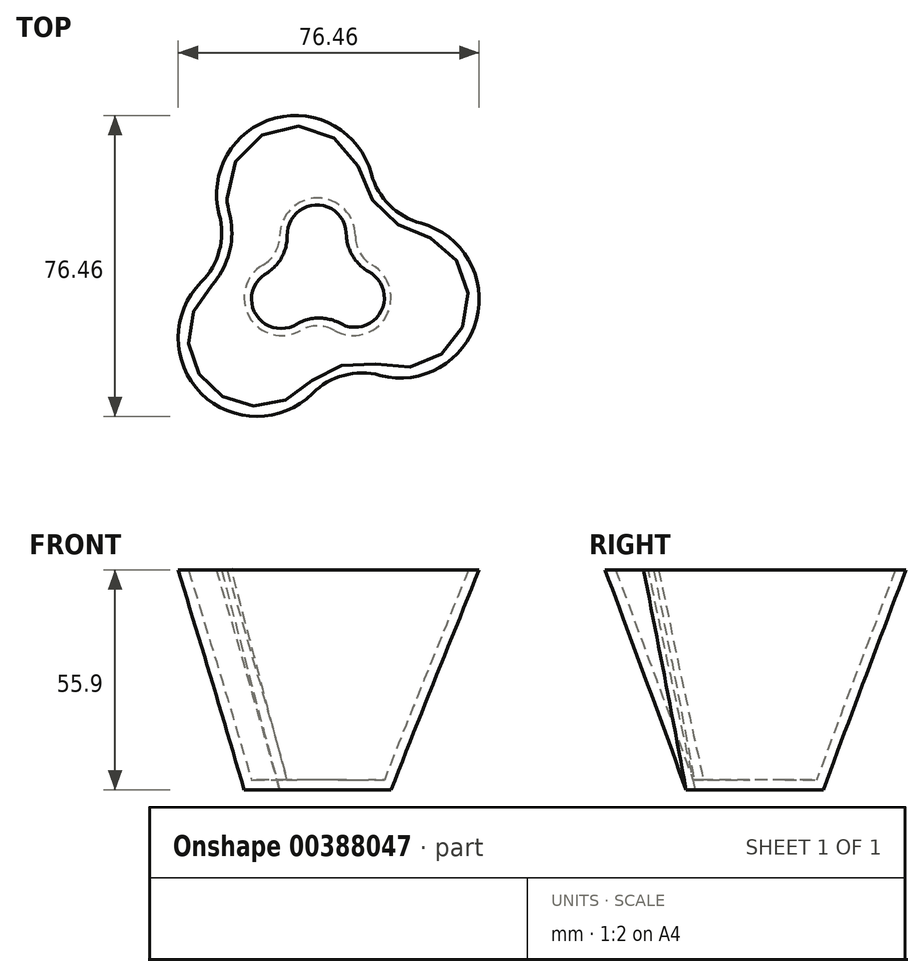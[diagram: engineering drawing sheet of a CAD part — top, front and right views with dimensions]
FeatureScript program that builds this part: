
annotation { "Feature Type Name" : "Feature", "Feature Type Description" : "" }
export const myFeature = defineFeature(function(context is Context, id is Id, definition is map)
    precondition{}
    {
        {
            var Q0;
            Q0=qCreatedBy(makeId("Top.planeOp"),FACE);
            var sketch = newSketch(context, id + "F0", { "sketchPlane" : qUnion([Q0])});
            skLineSegment(sketch, "E0", {"start": v(-8.66, -5) * mm, "end": v(-9.06, -5.23) * mm});
            skArc(sketch, "E1", {"start": v(-13.87, 3.09) * mm, "mid": v(-17.38, -10.04) * mm, "end": v(-4.26, -13.55) * mm});
            skArc(sketch, "E2.1.1", {"start": v(4.26, -13.55) * mm, "mid": v(17.38, -10.04) * mm, "end": v(13.87, 3.09) * mm});
            skArc(sketch, "E2.2.1", {"start": v(9.6, 10.47) * mm, "mid": v(0, 20.07) * mm, "end": v(-9.6, 10.47) * mm});
            skPoint(sketch, "E2.center", {"position": v(0, 0) * mm});
            skArc(sketch, "E3", {"start": v(4.26, -13.55) * mm, "mid": v(0, -12.41) * mm, "end": v(-4.26, -13.55) * mm});
            skArc(sketch, "E4", {"start": v(13.87, 3.09) * mm, "mid": v(10.75, 6.2) * mm, "end": v(9.6, 10.47) * mm});
            skArc(sketch, "E5", {"start": v(-13.87, 3.09) * mm, "mid": v(-10.75, 6.2) * mm, "end": v(-9.6, 10.47) * mm});
            skLineSegment(sketch, "E6.trimOffspring", {"start": v(-17.38, -10.04) * mm, "end": v(-34.64, -20) * mm});
            skPoint(sketch, "E7.end.orphan", {"position": v(2.4, -9.7) * mm});
            skPoint(sketch, "E8.orphan", {"position": v(-9.6, 2.78) * mm});
            skPoint(sketch, "E9.orphan", {"position": v(-7.21, 6.93) * mm});
            skLineSegment(sketch, "E10.trimOffspring", {"start": v(0, 20.07) * mm, "end": v(0, 40) * mm});
            skPoint(sketch, "E11.orphan", {"position": v(7.21, 6.93) * mm});
            skLineSegment(sketch, "E12.trimOffspring", {"start": v(17.38, -10.04) * mm, "end": v(34.64, -20) * mm});
            skSolve(sketch);
        }
        {
            var Q0;
            Q0=qCreatedBy(makeId("Top.planeOp"),FACE);
            cPlane(context, id + "F1", {"entities" : qUnion([Q0]), "cplaneType" : CPlaneType.OFFSET, "offset" : 55.9 * mm, "width" : 150 * mm, "height" : 150 * mm});
        }
        {
            var Q0;
            Q0=qCreatedBy(id+"F1.planeOp",FACE);
            var sketch = newSketch(context, id + "F2", { "sketchPlane" : qUnion([Q0])});
            skArc(sketch, "E13.0", {"start": v(13.68, 26.22) * mm, "mid": v(-10.82, 40.37) * mm, "end": v(-24.96, 15.87) * mm});
            skArc(sketch, "E14.0", {"start": v(26.22, 13.68) * mm, "mid": v(18.27, 18.27) * mm, "end": v(13.68, 26.22) * mm});
            skArc(sketch, "E15.0", {"start": v(15.87, -24.96) * mm, "mid": v(40.37, -10.82) * mm, "end": v(26.22, 13.68) * mm});
            skArc(sketch, "E16.0", {"start": v(15.87, -24.96) * mm, "mid": v(6.69, -24.96) * mm, "end": v(-1.27, -29.55) * mm});
            skArc(sketch, "E17.0", {"start": v(-29.55, -1.27) * mm, "mid": v(-29.55, -29.55) * mm, "end": v(-1.27, -29.55) * mm});
            skArc(sketch, "E18.0", {"start": v(-29.55, -1.27) * mm, "mid": v(-24.96, 6.69) * mm, "end": v(-24.96, 15.87) * mm});
            skPoint(sketch, "E19", {"position": v(0, 0) * mm});
            skPoint(sketch, "E20.orphan", {"position": v(18.27, 18.27) * mm});
            skPoint(sketch, "E21.end.orphan", {"position": v(-29.55, -29.55) * mm});
            skPoint(sketch, "E22.start.orphan", {"position": v(-24.96, 6.69) * mm});
            skPoint(sketch, "E23.trimOffspring.end.orphan", {"position": v(40.37, -10.82) * mm});
            skSolve(sketch);
        }
        {
            var Q0;
            {var subQ3=sQuery(id+"F0.wireOp",EDGE,"E3");Q0=makeQuery(id+"F0.imprint","IMPRINT",FACE,{"disambiguationData":[TD([[makeQuery(id+"F0.imprint","IMPRINT",EDGE,{"derivedFrom":subQ3}),-1.0]])]});}
            var Q1;
            Q1=makeQuery(id+"F2.imprint","IMPRINT",FACE,{"disambiguationData":[TD([[makeQuery(id+"F2.imprint","IMPRINT",EDGE,{"derivedFrom":sQuery(id+"F2.wireOp",EDGE,"E13.0")}),1.0]])]});
            loft(context, id + "F3", {"sheetProfilesArray" : [{ "sheetProfileEntities" : qUnion([Q0]) }, { "sheetProfileEntities" : qUnion([Q1]) }]});
        }
        {
            var Q0;
            Q0=makeQuery(id+"F3.opLoft","CAP_FACE",FACE,{"disambiguationData":[OSD([makeQuery(id+"F2.imprint","IMPRINT",FACE,{"disambiguationData":[TD([[makeQuery(id+"F2.imprint","IMPRINT",EDGE,{"derivedFrom":sQuery(id+"F2.wireOp",EDGE,"E13.0")}),1.0]])]})])],"isStart":true});
            shell(context, id + "F4", {"entities" : qUnion([Q0]), "thickness" : 2.5 * mm});
        }
    });
